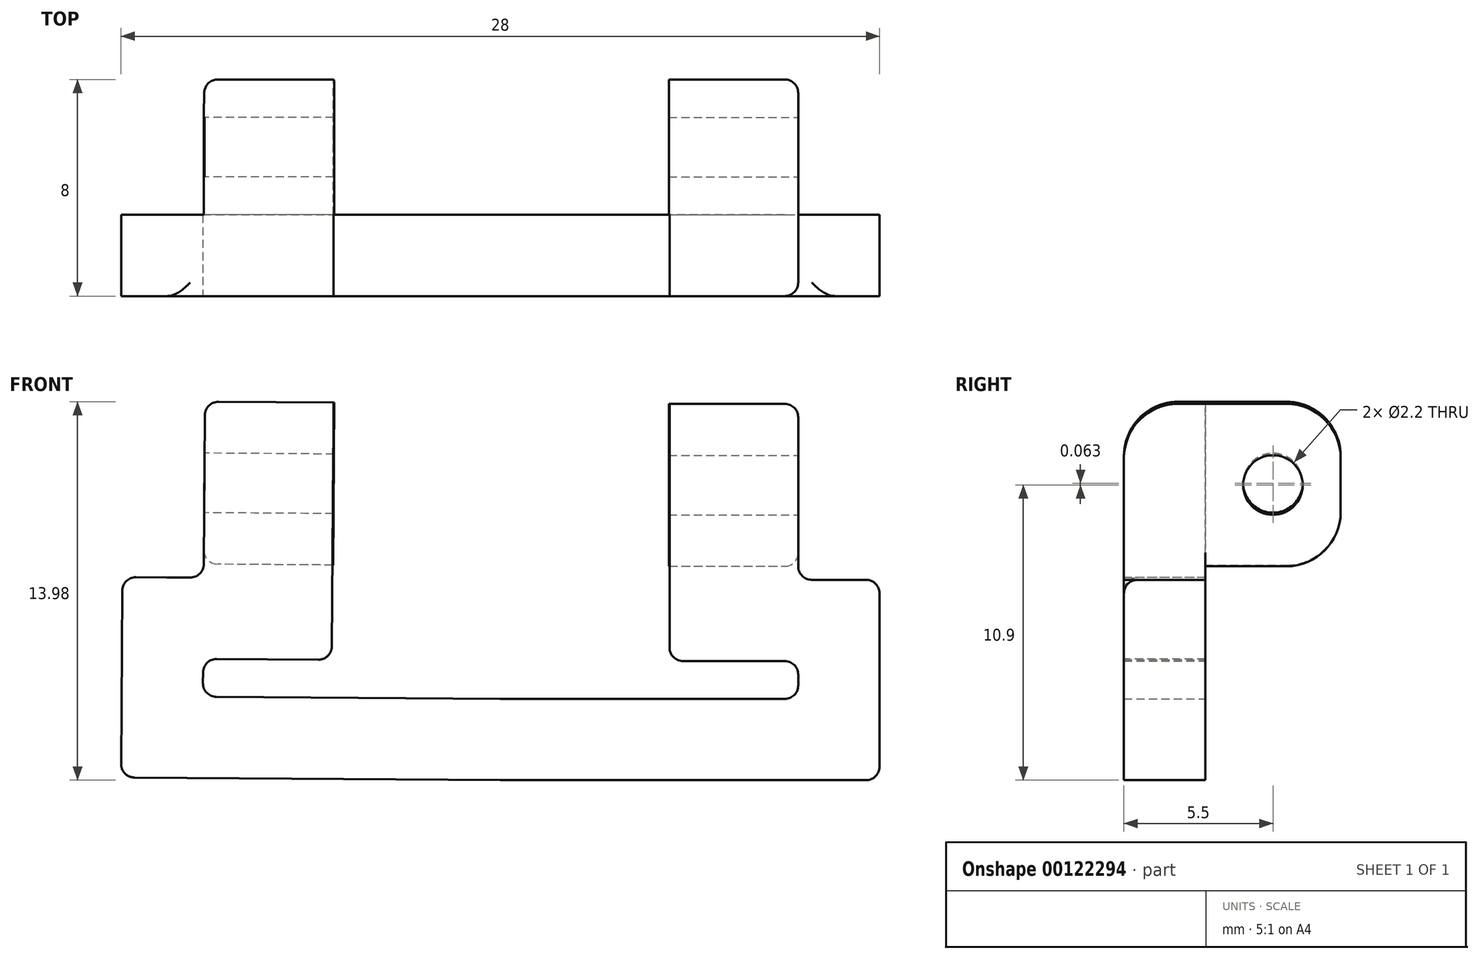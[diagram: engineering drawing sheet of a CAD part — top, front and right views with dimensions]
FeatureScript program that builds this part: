
annotation { "Feature Type Name" : "Feature", "Feature Type Description" : "" }
export const myFeature = defineFeature(function(context is Context, id is Id, definition is map)
    precondition{}
    {
        {
            var Q0;
            Q0=qCreatedBy(makeId("Front.planeOp"),FACE);
            var sketch = newSketch(context, id + "F0", { "sketchPlane" : qUnion([Q0])});
            skLineSegment(sketch, "E0", {"start": v(0, 0) * mm, "end": v(14, 0) * mm});
            skLineSegment(sketch, "E1", {"start": v(14, 0) * mm, "end": v(14, 7.4) * mm});
            skLineSegment(sketch, "E2", {"start": v(14, 7.4) * mm, "end": v(11, 7.4) * mm});
            skLineSegment(sketch, "E3", {"start": v(11, 7.4) * mm, "end": v(11, 13.9) * mm});
            skLineSegment(sketch, "E4", {"start": v(11, 13.9) * mm, "end": v(6.25, 13.9) * mm});
            skLineSegment(sketch, "E5", {"start": v(6.25, 13.9) * mm, "end": v(6.25, 4.4) * mm});
            skLineSegment(sketch, "E6", {"start": v(6.25, 4.4) * mm, "end": v(11, 4.4) * mm});
            skLineSegment(sketch, "E7", {"start": v(11, 4.4) * mm, "end": v(11, 3) * mm});
            skLineSegment(sketch, "E8", {"start": v(11, 3) * mm, "end": v(0.01, 3) * mm});
            skLineSegment(sketch, "E9", {"start": v(0.01, 3) * mm, "end": v(0, 0) * mm});
            skLineSegment(sketch, "E10.MirrorCS", {"start": v(-0.01, 3) * mm, "end": v(0, 0) * mm});
            skSolve(sketch);
        }
        {
            var Q0;
            Q0 = qSketchRegion(id + "F0", true);
            var Q1;
            Q1=makeQuery(id+"F0.imprint","IMPRINT",FACE,{"disambiguationData":[TD([[makeQuery(id+"F0.imprint","IMPRINT",EDGE,{"derivedFrom":sQuery(id+"F0.wireOp",EDGE,"c9ca4887-6162-4779-8af6-7972fd4a53910.MirrorCS")}),-1.0]])]});
            extrude(context, id + "F1", {"entities" : qUnion([Q0, Q1]), "depth" : 3 * mm});
        }
        {
            var Q0;
            Q0=makeQuery(id+"F1.opExtrude","SWEPT_FACE",FACE,{"disambiguationData":[OSD([sQuery(id+"F0.wireOp",EDGE,"E3")])]});
            var sketch = newSketch(context, id + "F2", { "sketchPlane" : qUnion([Q0])});
            skLineSegment(sketch, "E11", {"start": v(0, 7.9) * mm, "end": v(5, 7.9) * mm});
            skLineSegment(sketch, "E12", {"start": v(5, 7.9) * mm, "end": v(5, 13.9) * mm});
            skLineSegment(sketch, "E13", {"start": v(5, 13.9) * mm, "end": v(0, 13.9) * mm});
            skPoint(sketch, "E14", {"position": v(2.5, 10.9) * mm});
            skSolve(sketch);
        }
        {
            var Q0;
            {var subQ0=sQuery(id+"F2.wireOp",EDGE,"E11");Q0=makeQuery(id+"F2.imprint","IMPRINT",FACE,{"disambiguationData":[TD([[makeQuery(id+"F2.imprint","IMPRINT",EDGE,{"derivedFrom":subQ0}),1.0]])]});}
            extrude(context, id + "F3", {"entities" : qUnion([Q0]), "operationType" : NewBodyOperationType.ADD, "oppositeDirection" : true, "depth" : 4.78 * mm});
        }
        {
            var Q0;
            Q0=sQuery(id+"F2.wireOp",VERTEX,"E14");
            var Q1;
            Q1=makeQuery(id+"F1.opExtrude","SWEPT_BODY",BODY,{"disambiguationData":[OSD([sQuery(id+"F0.wireOp",EDGE,"E0"),sQuery(id+"F0.wireOp",EDGE,"E1"),sQuery(id+"F0.wireOp",EDGE,"E2"),sQuery(id+"F0.wireOp",EDGE,"E3"),sQuery(id+"F0.wireOp",EDGE,"E4"),sQuery(id+"F0.wireOp",EDGE,"E5"),sQuery(id+"F0.wireOp",EDGE,"E6"),sQuery(id+"F0.wireOp",EDGE,"E7"),sQuery(id+"F0.wireOp",EDGE,"E8"),sQuery(id+"F0.wireOp",EDGE,"E9")])]});
            hole(context, id + "F4", {"style" : HoleStyle.SIMPLE, "endStyle" : HoleEndStyle.THROUGH, "holeDiameter" : 2.2 * mm, "locations" : qUnion([Q0]), "scope" : qUnion([Q1]), "isTappedThrough" : true});
        }
        {
            var Q0;
            Q0=makeQuery(id+"F3.opExtrude","SWEPT_EDGE",EDGE,{"disambiguationData":[OSD([sQuery(id+"F2.wireOp",EDGE,"E12"),sQuery(id+"F2.wireOp",EDGE,"E13")])]});
            var Q1;
            Q1=makeQuery(id+"F3.opExtrude","SWEPT_EDGE",EDGE,{"disambiguationData":[OSD([sQuery(id+"F2.wireOp",EDGE,"E11"),sQuery(id+"F2.wireOp",EDGE,"E12")])]});
            var Q2;
            Q2=makeQuery(id+"F1.opExtrude","CAP_EDGE",EDGE,{"disambiguationData":[OSD([sQuery(id+"F0.wireOp",EDGE,"E4")])],"isStart":false});
            fillet(context, id + "F5", {"entities" : qUnion([Q0, Q1, Q2]), "radius" : 2 * mm, "tangentPropagation" : true, "allowEdgeOverflow" : false});
        }
        {
            var Q0;
            Q0=makeQuery(id+"F1.opExtrude","SWEPT_EDGE",EDGE,{"disambiguationData":[OSD([sQuery(id+"F0.wireOp",EDGE,"E1"),sQuery(id+"F0.wireOp",EDGE,"E2")])]});
            var Q1;
            Q1=makeQuery(id+"F1.opExtrude","SWEPT_EDGE",EDGE,{"disambiguationData":[OSD([sQuery(id+"F0.wireOp",EDGE,"E5"),sQuery(id+"F0.wireOp",EDGE,"E6")])]});
            var Q2;
            Q2=makeQuery(id+"F1.opExtrude","SWEPT_EDGE",EDGE,{"disambiguationData":[OSD([sQuery(id+"F0.wireOp",EDGE,"E0"),sQuery(id+"F0.wireOp",EDGE,"E1")])]});
            var Q3;
            Q3=makeQuery(id+"F1.opExtrude","SWEPT_EDGE",EDGE,{"disambiguationData":[OSD([sQuery(id+"F0.wireOp",EDGE,"E6"),sQuery(id+"F0.wireOp",EDGE,"E7")])]});
            var Q4;
            Q4=makeQuery(id+"F1.opExtrude","SWEPT_EDGE",EDGE,{"disambiguationData":[OSD([sQuery(id+"F0.wireOp",EDGE,"E7"),sQuery(id+"F0.wireOp",EDGE,"E8")])]});
            var Q5;
            Q5=makeQuery(id+"F1.opExtrude","SWEPT_EDGE",EDGE,{"disambiguationData":[OSD([sQuery(id+"F0.wireOp",EDGE,"E2"),sQuery(id+"F0.wireOp",EDGE,"E3")])]});
            var Q6;
            Q6=makeQuery(id+"F3.boolean.opBoolean","MERGE",EDGE,{"derivedFrom":[makeQuery(id+"F1.opExtrude","SWEPT_EDGE",EDGE,{"disambiguationData":[OSD([sQuery(id+"F0.wireOp",EDGE,"E3"),sQuery(id+"F0.wireOp",EDGE,"E4")])]}),makeQuery(id+"F3.opExtrude","CAP_EDGE",EDGE,{"disambiguationData":[OSD([sQuery(id+"F2.wireOp",EDGE,"E13")])],"isStart":true})]});
            fillet(context, id + "F6", {"entities" : qUnion([Q0, Q1, Q2, Q3, Q4, Q5, Q6]), "radius" : 0.5 * mm, "tangentPropagation" : true, "allowEdgeOverflow" : false});
        }
        {
            var Q0;
            Q0=makeQuery(id+"F1.opExtrude","SWEPT_BODY",BODY,{"disambiguationData":[OSD([sQuery(id+"F0.wireOp",EDGE,"E0"),sQuery(id+"F0.wireOp",EDGE,"E1"),sQuery(id+"F0.wireOp",EDGE,"E2"),sQuery(id+"F0.wireOp",EDGE,"E3"),sQuery(id+"F0.wireOp",EDGE,"E4"),sQuery(id+"F0.wireOp",EDGE,"E5"),sQuery(id+"F0.wireOp",EDGE,"E6"),sQuery(id+"F0.wireOp",EDGE,"E7"),sQuery(id+"F0.wireOp",EDGE,"E8"),sQuery(id+"F0.wireOp",EDGE,"E9")])]});
            var Q1;
            Q1=makeQuery(id+"F1.opExtrude","SWEPT_FACE",FACE,{"disambiguationData":[OSD([sQuery(id+"F0.wireOp",EDGE,"E9")])]});
            mirror(context, id + "F7", {"operationType" : NewBodyOperationType.ADD, "entities" : qUnion([Q0]), "mirrorPlane" : qUnion([Q1])});
        }
    });
